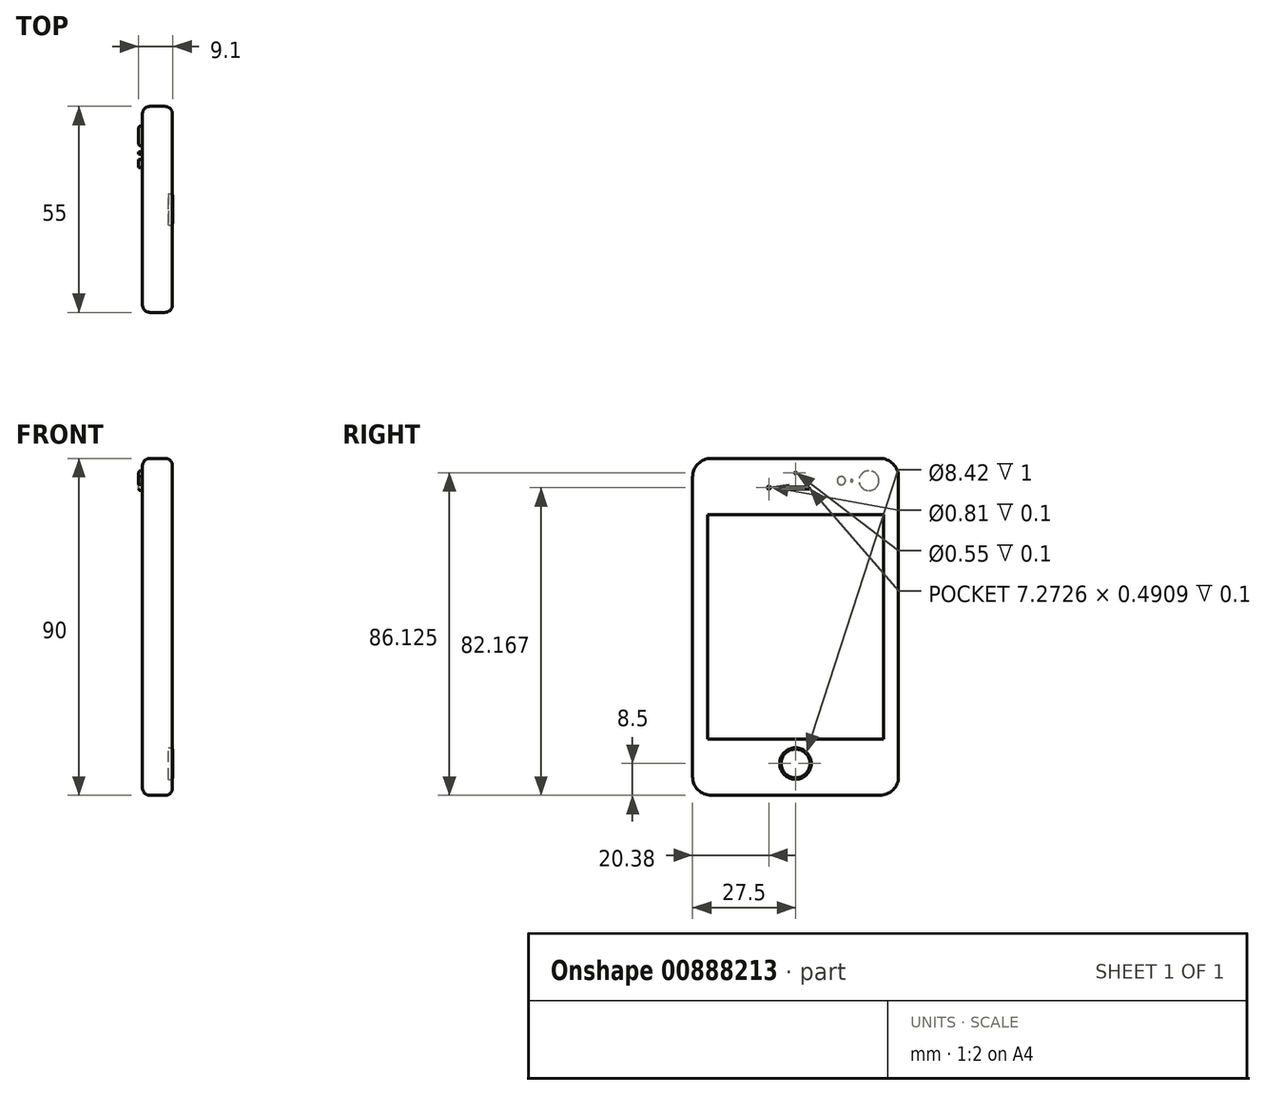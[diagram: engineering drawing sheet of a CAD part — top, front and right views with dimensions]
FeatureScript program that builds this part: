
annotation { "Feature Type Name" : "Feature", "Feature Type Description" : "" }
export const myFeature = defineFeature(function(context is Context, id is Id, definition is map)
    precondition{}
    {
        {
            var Q0;
            Q0=qCreatedBy(makeId("Right.planeOp"),FACE);
            var sketch = newSketch(context, id + "F0", { "sketchPlane" : qUnion([Q0])});
            skLineSegment(sketch, "E0.bottom", {"start": v(27.5, -45) * mm, "end": v(-27.5, -45) * mm});
            skLineSegment(sketch, "E0.top", {"start": v(27.5, 45) * mm, "end": v(-27.5, 45) * mm});
            skLineSegment(sketch, "E0.left", {"start": v(27.5, -45) * mm, "end": v(27.5, 45) * mm});
            skLineSegment(sketch, "E0.right", {"start": v(-27.5, -45) * mm, "end": v(-27.5, 45) * mm});
            skPoint(sketch, "E0.middle", {"position": v(0, 0) * mm});
            skSolve(sketch);
        }
        {
            var Q0;
            Q0 = qSketchRegion(id + "F0", true);
            extrude(context, id + "F1", {"entities" : qUnion([Q0]), "endBound" : BoundingType.SYMMETRIC, "depth" : 8 * mm, "offsetDistance" : 25 * mm});
        }
        {
            var Q0;
            Q0=makeQuery(id+"F1.opExtrude","SWEPT_EDGE",EDGE,{"disambiguationData":[OSD([sQuery(id+"F0.wireOp",EDGE,"E0.top"),sQuery(id+"F0.wireOp",EDGE,"E0.right")])]});
            var Q1;
            Q1=makeQuery(id+"F1.opExtrude","SWEPT_EDGE",EDGE,{"disambiguationData":[OSD([sQuery(id+"F0.wireOp",EDGE,"E0.bottom"),sQuery(id+"F0.wireOp",EDGE,"E0.right")])]});
            var Q2;
            Q2=makeQuery(id+"F1.opExtrude","SWEPT_EDGE",EDGE,{"disambiguationData":[OSD([sQuery(id+"F0.wireOp",EDGE,"E0.top"),sQuery(id+"F0.wireOp",EDGE,"E0.left")])]});
            var Q3;
            Q3=makeQuery(id+"F1.opExtrude","SWEPT_EDGE",EDGE,{"disambiguationData":[OSD([sQuery(id+"F0.wireOp",EDGE,"E0.bottom"),sQuery(id+"F0.wireOp",EDGE,"E0.left")])]});
            fillet(context, id + "F2", {"entities" : qUnion([Q0, Q1, Q2, Q3]), "radius" : 5 * mm, "tangentPropagation" : true, "allowEdgeOverflow" : false});
        }
        {
            var Q0;
            Q0=makeQuery(id+"F1.opExtrude","CAP_EDGE",EDGE,{"disambiguationData":[OSD([sQuery(id+"F0.wireOp",EDGE,"E0.bottom")])],"isStart":false});
            var Q1;
            Q1=makeQuery(id+"F1.opExtrude","CAP_EDGE",EDGE,{"disambiguationData":[OSD([sQuery(id+"F0.wireOp",EDGE,"E0.top")])],"isStart":true});
            fillet(context, id + "F3", {"entities" : qUnion([Q0, Q1]), "radius" : 2 * mm, "tangentPropagation" : true, "allowEdgeOverflow" : false});
        }
        {
            var Q0;
            Q0=makeQuery(id+"F1.opExtrude","CAP_FACE",FACE,{"disambiguationData":[OSD([sQuery(id+"F0.wireOp",EDGE,"E0.bottom"),sQuery(id+"F0.wireOp",EDGE,"E0.top"),sQuery(id+"F0.wireOp",EDGE,"E0.left"),sQuery(id+"F0.wireOp",EDGE,"E0.right")])],"isStart":false});
            var sketch = newSketch(context, id + "F4", { "sketchPlane" : qUnion([Q0])});
            skLineSegment(sketch, "E1.bottom", {"start": v(23.5, -30) * mm, "end": v(-23.5, -30) * mm});
            skLineSegment(sketch, "E1.top", {"start": v(23.5, 30) * mm, "end": v(-23.5, 30) * mm});
            skLineSegment(sketch, "E1.left", {"start": v(23.5, -30) * mm, "end": v(23.5, 30) * mm});
            skLineSegment(sketch, "E1.right", {"start": v(-23.5, -30) * mm, "end": v(-23.5, 30) * mm});
            skPoint(sketch, "E1.middle", {"position": v(0, 0) * mm});
            skPoint(sketch, "E2", {"position": v(0, -30) * mm});
            skPoint(sketch, "E3", {"position": v(0, -43) * mm});
            skPoint(sketch, "E4", {"position": v(0, -36.5) * mm});
            skCircle(sketch, "E5", {"center": v(0, -36.5) * mm, "radius": 4.21 * mm});
            skSolve(sketch);
        }
        {
            var Q0;
            Q0=makeQuery(id+"F4.imprint","IMPRINT",FACE,{"disambiguationData":[TD([[makeQuery(id+"F4.imprint","IMPRINT",EDGE,{"derivedFrom":sQuery(id+"F4.wireOp",EDGE,"E5")}),1.0]])]});
            extrude(context, id + "F5", {"entities" : qUnion([Q0]), "operationType" : NewBodyOperationType.REMOVE, "oppositeDirection" : true, "depth" : 1 * mm, "offsetDistance" : 25 * mm});
        }
        {
            var Q0;
            Q0=makeQuery(id+"F4.imprint","IMPRINT",FACE,{"disambiguationData":[TD([[makeQuery(id+"F4.imprint","IMPRINT",EDGE,{"derivedFrom":sQuery(id+"F4.wireOp",EDGE,"E5")}),1.0]])]});
            var sketch = newSketch(context, id + "F6", { "sketchPlane" : qUnion([Q0])});
            skCircle(sketch, "E6", {"center": v(0, -36.5) * mm, "radius": 3.85 * mm});
            skSolve(sketch);
        }
        {
            var Q0;
            Q0=makeQuery(id+"F6.imprint","IMPRINT",FACE,{"disambiguationData":[TD([[makeQuery(id+"F6.imprint","IMPRINT",EDGE,{"derivedFrom":sQuery(id+"F6.wireOp",EDGE,"E6")}),1.0]])]});
            extrude(context, id + "F7", {"entities" : qUnion([Q0]), "depth" : 0.1 * mm, "offsetDistance" : 25 * mm});
        }
        {
            var Q0;
            Q0=makeQuery(id+"F4.imprint","IMPRINT",FACE,{"disambiguationData":[TD([[makeQuery(id+"F4.imprint","IMPRINT",EDGE,{"derivedFrom":sQuery(id+"F4.wireOp",EDGE,"E1.bottom")}),-1.0]])]});
            var sketch = newSketch(context, id + "F8", { "sketchPlane" : qUnion([Q0])});
            skLineSegment(sketch, "E7.bottom", {"start": v(3.64, 36.89) * mm, "end": v(-3.64, 36.89) * mm});
            skLineSegment(sketch, "E7.top", {"start": v(3.64, 37.38) * mm, "end": v(-3.64, 37.38) * mm});
            skLineSegment(sketch, "E7.left", {"start": v(3.64, 36.89) * mm, "end": v(3.64, 37.38) * mm});
            skLineSegment(sketch, "E7.right", {"start": v(-3.64, 36.89) * mm, "end": v(-3.64, 37.38) * mm});
            skPoint(sketch, "E7.middle", {"position": v(0, 37.13) * mm});
            skSolve(sketch);
        }
        {
            var Q0;
            Q0 = qSketchRegion(id + "F8", true);
            extrude(context, id + "F9", {"entities" : qUnion([Q0]), "operationType" : NewBodyOperationType.REMOVE, "oppositeDirection" : true, "depth" : 0.1 * mm, "offsetDistance" : 25 * mm});
        }
        {
            var Q0;
            Q0=makeQuery(id+"F4.imprint","IMPRINT",FACE,{"disambiguationData":[TD([[makeQuery(id+"F4.imprint","IMPRINT",EDGE,{"derivedFrom":sQuery(id+"F4.wireOp",EDGE,"E1.bottom")}),1.0]])]});
            var sketch = newSketch(context, id + "F10", { "sketchPlane" : qUnion([Q0])});
            skCircle(sketch, "E8", {"center": v(-7.12, 37.17) * mm, "radius": 0.4 * mm});
            skSolve(sketch);
        }
        {
            var Q0;
            Q0 = qSketchRegion(id + "F10", true);
            extrude(context, id + "F11", {"entities" : qUnion([Q0]), "operationType" : NewBodyOperationType.REMOVE, "oppositeDirection" : true, "depth" : 0.1 * mm, "offsetDistance" : 25 * mm});
        }
        {
            var Q0;
            Q0=makeQuery(id+"F4.imprint","IMPRINT",FACE,{"disambiguationData":[TD([[makeQuery(id+"F4.imprint","IMPRINT",EDGE,{"derivedFrom":sQuery(id+"F4.wireOp",EDGE,"E1.bottom")}),1.0]])]});
            var sketch = newSketch(context, id + "F12", { "sketchPlane" : qUnion([Q0])});
            skCircle(sketch, "E9", {"center": v(0, 41.12) * mm, "radius": 0.27 * mm});
            skSolve(sketch);
        }
        {
            var Q0;
            Q0 = qSketchRegion(id + "F12", true);
            extrude(context, id + "F13", {"entities" : qUnion([Q0]), "operationType" : NewBodyOperationType.REMOVE, "oppositeDirection" : true, "depth" : 0.1 * mm, "offsetDistance" : 25 * mm});
        }
        {
            var Q0;
            Q0=makeQuery(id+"F4.imprint","IMPRINT",FACE,{"disambiguationData":[TD([[makeQuery(id+"F4.imprint","IMPRINT",EDGE,{"derivedFrom":sQuery(id+"F4.wireOp",EDGE,"E1.bottom")}),-1.0]])]});
            extrude(context, id + "F14", {"entities" : qUnion([Q0]), "operationType" : NewBodyOperationType.REMOVE, "oppositeDirection" : true, "depth" : 0 * mm, "offsetDistance" : 25 * mm});
        }
        {
            var Q0;
            Q0=makeQuery(id+"F1.opExtrude","CAP_FACE",FACE,{"disambiguationData":[OSD([sQuery(id+"F0.wireOp",EDGE,"E0.bottom"),sQuery(id+"F0.wireOp",EDGE,"E0.top"),sQuery(id+"F0.wireOp",EDGE,"E0.left"),sQuery(id+"F0.wireOp",EDGE,"E0.right")])],"isStart":true});
            var sketch = newSketch(context, id + "F15", { "sketchPlane" : qUnion([Q0])});
            skLineSegment(sketch, "E10", {"start": v(-25.5, 35.2) * mm, "end": v(25.5, 35.2) * mm});
            skLineSegment(sketch, "E11", {"start": v(25.5, 35.2) * mm, "end": v(25.5, 33.84) * mm});
            skLineSegment(sketch, "E12", {"start": v(25.5, 33.84) * mm, "end": v(-25.5, 33.84) * mm});
            skLineSegment(sketch, "E13", {"start": v(-25.5, 33.84) * mm, "end": v(-25.5, 35.2) * mm});
            skLineSegment(sketch, "E14.MirrorCS", {"start": v(25.5, -33.84) * mm, "end": v(-25.5, -33.84) * mm});
            skLineSegment(sketch, "E15.MirrorCS", {"start": v(-25.5, -35.2) * mm, "end": v(25.5, -35.2) * mm});
            skSolve(sketch);
        }
        {
            var Q0;
            {var subQ5=sQuery(id+"F15.wireOp",EDGE,"E10");Q0=makeQuery(id+"F15.imprint","IMPRINT",FACE,{"disambiguationData":[TD([[makeQuery(id+"F15.imprint","IMPRINT",EDGE,{"derivedFrom":subQ5}),1.0]])]});}
            var sketch = newSketch(context, id + "F16", { "sketchPlane" : qUnion([Q0])});
            skCircle(sketch, "E16", {"center": v(-19.61, 39.04) * mm, "radius": 2.65 * mm});
            skCircle(sketch, "E17", {"center": v(-15, 39.04) * mm, "radius": 0.31 * mm});
            skCircle(sketch, "E18", {"center": v(-12.24, 39.04) * mm, "radius": 1.09 * mm});
            skSolve(sketch);
        }
        {
            var Q0;
            Q0 = qSketchRegion(id + "F16", true);
            extrude(context, id + "F17", {"entities" : qUnion([Q0]), "operationType" : NewBodyOperationType.ADD, "depth" : 1 * mm, "offsetDistance" : 25 * mm});
        }
        {
            var Q0;
            Q0=makeQuery(id+"F17.opExtrude","CAP_EDGE",EDGE,{"disambiguationData":[OSD([sQuery(id+"F16.wireOp",EDGE,"E16")])],"isStart":false});
            fillet(context, id + "F18", {"entities" : qUnion([Q0]), "radius" : 0.5 * mm, "tangentPropagation" : true, "allowEdgeOverflow" : false});
        }
    });
